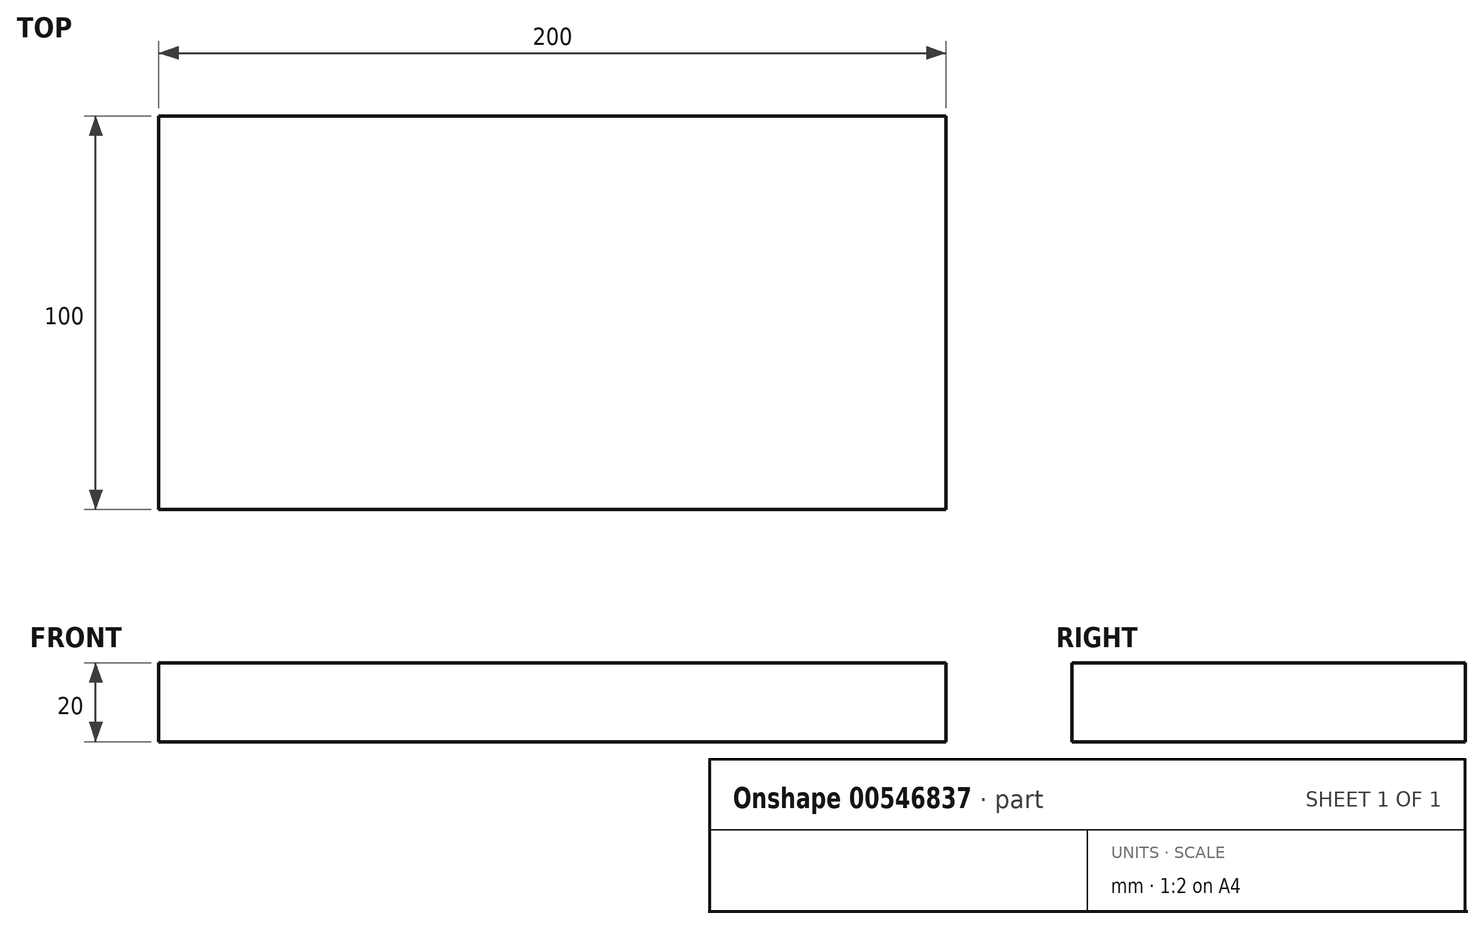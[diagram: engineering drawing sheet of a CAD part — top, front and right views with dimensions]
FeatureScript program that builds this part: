
annotation { "Feature Type Name" : "Feature", "Feature Type Description" : "" }
export const myFeature = defineFeature(function(context is Context, id is Id, definition is map)
    precondition{}
    {
        {
            var Q0;
            Q0=qCreatedBy(makeId("Top.planeOp"),FACE);
            var sketch = newSketch(context, id + "F0", { "sketchPlane" : qUnion([Q0])});
            skLineSegment(sketch, "E0.bottom", {"start": v(-101.4, 50.15) * mm, "end": v(98.6, 50.15) * mm});
            skLineSegment(sketch, "E0.top", {"start": v(-101.4, -49.85) * mm, "end": v(98.6, -49.85) * mm});
            skLineSegment(sketch, "E0.left", {"start": v(-101.4, 50.15) * mm, "end": v(-101.4, -49.85) * mm});
            skLineSegment(sketch, "E0.right", {"start": v(98.6, 50.15) * mm, "end": v(98.6, -49.85) * mm});
            skSolve(sketch);
        }
        {
            var Q0;
            Q0 = qSketchRegion(id + "F0", true);
            extrude(context, id + "F1", {"entities" : qUnion([Q0]), "depth" : 20 * mm, "offsetDistance" : 25 * mm});
        }
    });
